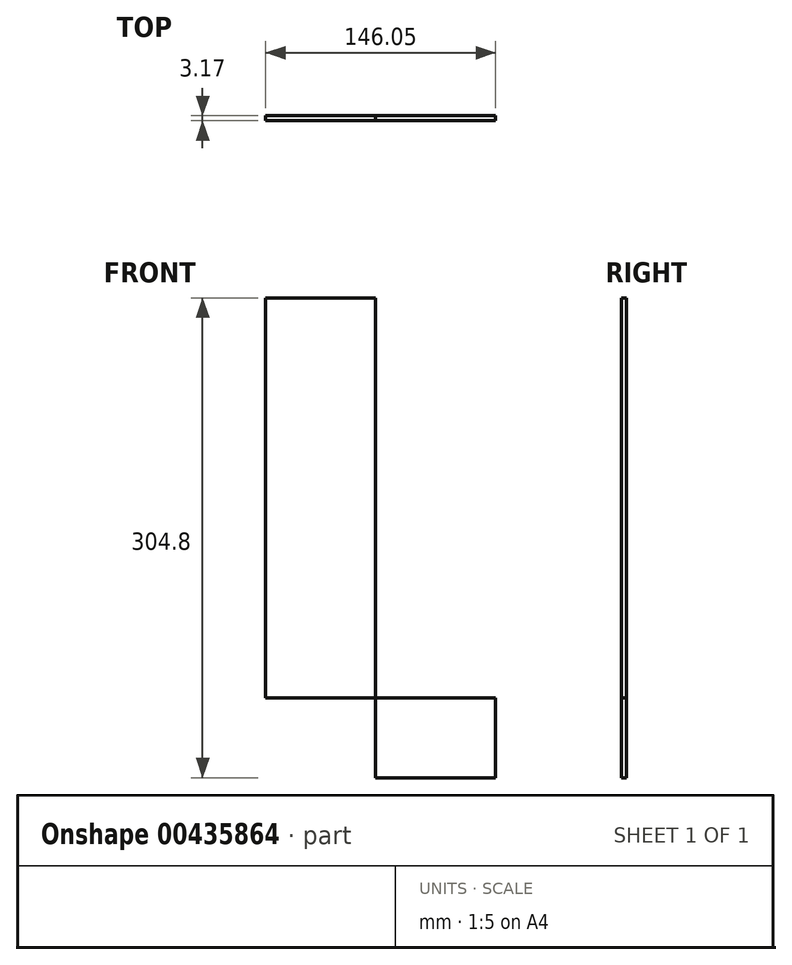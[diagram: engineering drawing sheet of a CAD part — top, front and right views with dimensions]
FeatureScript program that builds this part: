
annotation { "Feature Type Name" : "Feature", "Feature Type Description" : "" }
export const myFeature = defineFeature(function(context is Context, id is Id, definition is map)
    precondition{}
    {
        {
            var Q0;
            Q0=qCreatedBy(makeId("Front.planeOp"),FACE);
            var sketch = newSketch(context, id + "F0", { "sketchPlane" : qUnion([Q0])});
            skLineSegment(sketch, "E0.bottom", {"start": v(0, 0) * mm, "end": v(-69.85, 0) * mm});
            skLineSegment(sketch, "E0.top", {"start": v(0, 304.8) * mm, "end": v(-69.85, 304.8) * mm});
            skLineSegment(sketch, "E0.left", {"start": v(0, 0) * mm, "end": v(0, 304.8) * mm});
            skLineSegment(sketch, "E0.right", {"start": v(-69.85, 0) * mm, "end": v(-69.85, 304.8) * mm});
            skLineSegment(sketch, "E1.bottom", {"start": v(-69.85, 0) * mm, "end": v(76.2, 0) * mm});
            skLineSegment(sketch, "E1.top", {"start": v(-69.85, 50.8) * mm, "end": v(76.2, 50.8) * mm});
            skLineSegment(sketch, "E1.left", {"start": v(-69.85, 0) * mm, "end": v(-69.85, 50.8) * mm});
            skLineSegment(sketch, "E1.right", {"start": v(76.2, 0) * mm, "end": v(76.2, 50.8) * mm});
            skSolve(sketch);
        }
        {
            var Q0;
            {var subQ0=sQuery(id+"F0.wireOp",EDGE,"E0.top");Q0=makeQuery(id+"F0.imprint","IMPRINT",FACE,{"disambiguationData":[TD([[makeQuery(id+"F0.imprint","IMPRINT",EDGE,{"derivedFrom":subQ0}),1.0]])]});}
            var Q1;
            {var subQ5=sQuery(id+"F0.wireOp",EDGE,"E1.left");Q1=makeQuery(id+"F0.imprint","IMPRINT",FACE,{"disambiguationData":[TD([[makeQuery(id+"F0.imprint","IMPRINT",EDGE,{"derivedFrom":subQ5}),-1.0]])]});}
            var Q2;
            {var subQ5=sQuery(id+"F0.wireOp",EDGE,"E1.right");Q2=makeQuery(id+"F0.imprint","IMPRINT",FACE,{"disambiguationData":[TD([[makeQuery(id+"F0.imprint","IMPRINT",EDGE,{"derivedFrom":subQ5}),1.0]])]});}
            extrude(context, id + "F1", {"entities" : qUnion([Q0, Q1, Q2]), "depth" : 3.17 * mm});
        }
    });
